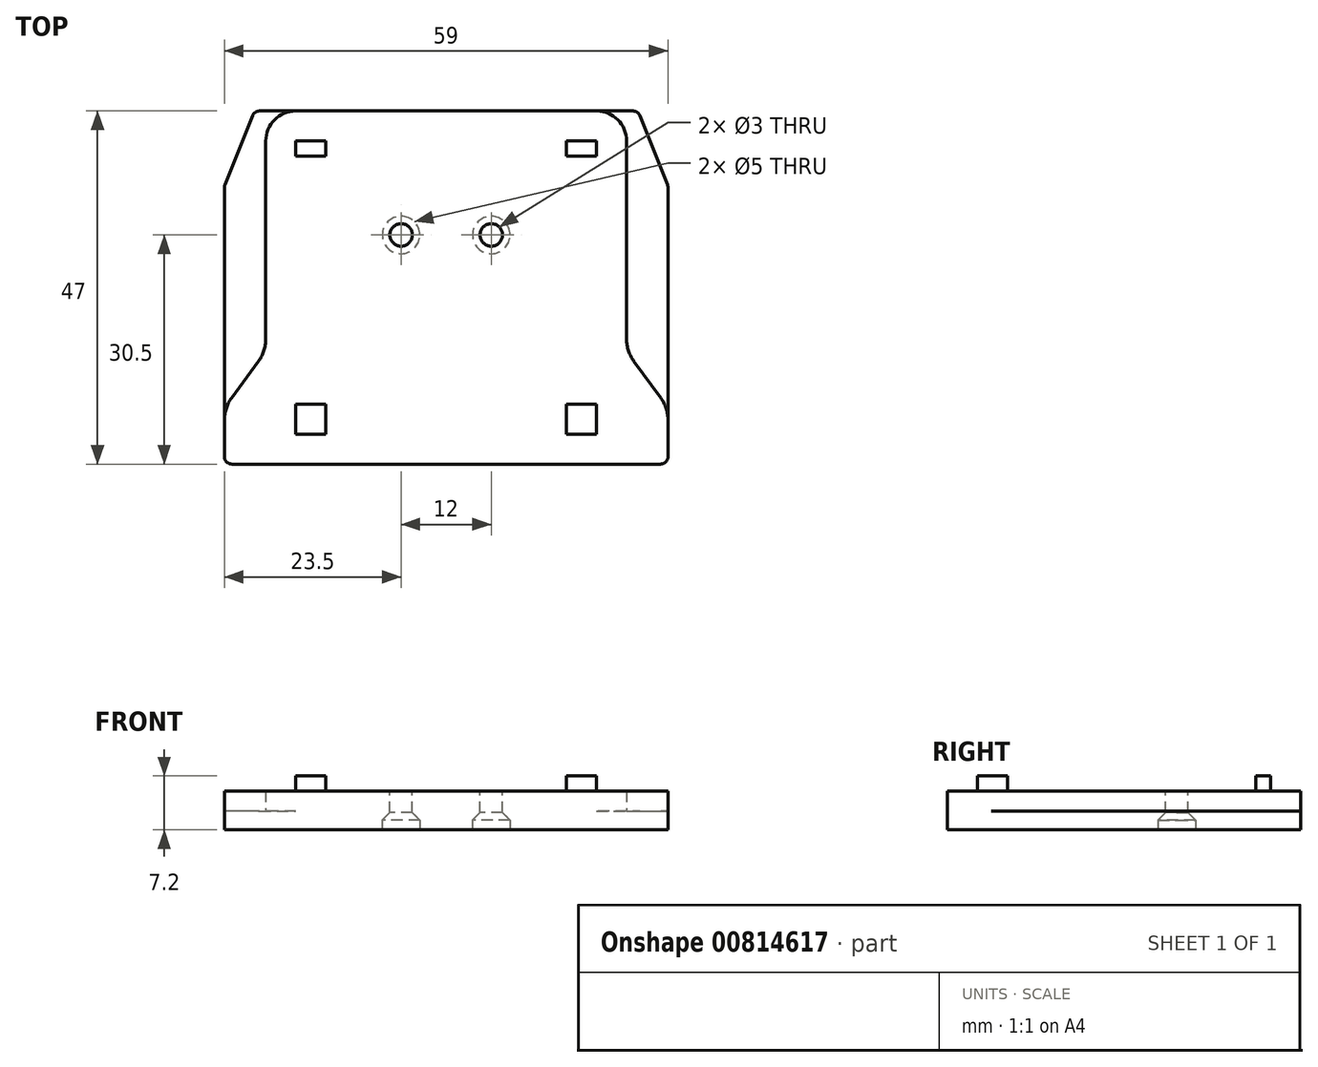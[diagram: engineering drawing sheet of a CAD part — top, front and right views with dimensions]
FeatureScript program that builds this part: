
annotation { "Feature Type Name" : "Feature", "Feature Type Description" : "" }
export const myFeature = defineFeature(function(context is Context, id is Id, definition is map)
    precondition{}
    {
        {
            var Q0;
            Q0=qCreatedBy(makeId("Top.planeOp"),FACE);
            var sketch = newSketch(context, id + "F0", { "sketchPlane" : qUnion([Q0])});
            skLineSegment(sketch, "E0.bottom", {"start": v(4, 0) * mm, "end": v(55, 0) * mm});
            skLineSegment(sketch, "E0.top", {"start": v(0, -47) * mm, "end": v(59, -47) * mm});
            skLineSegment(sketch, "E0.left", {"start": v(0, -10) * mm, "end": v(0, -47) * mm});
            skLineSegment(sketch, "E0.right", {"start": v(59, -10) * mm, "end": v(59, -47) * mm});
            skLineSegment(sketch, "E1", {"start": v(4, 0) * mm, "end": v(0, -10) * mm});
            skPoint(sketch, "E2.orphan", {"position": v(0, 0) * mm});
            skLineSegment(sketch, "E3", {"start": v(55, 0) * mm, "end": v(59, -10) * mm});
            skPoint(sketch, "E4.orphan", {"position": v(59, 0) * mm});
            skSolve(sketch);
        }
        {
            var Q0;
            Q0=makeQuery(id+"F0.imprint","IMPRINT",FACE,{"disambiguationData":[TD([[makeQuery(id+"F0.imprint","IMPRINT",EDGE,{"derivedFrom":sQuery(id+"F0.wireOp",EDGE,"E0.bottom")}),-1.0]])]});
            extrude(context, id + "F1", {"entities" : qUnion([Q0]), "depth" : 2.5 * mm, "offsetDistance" : 25 * mm});
        }
        {
            var Q0;
            Q0=makeQuery(id+"F1.opExtrude","CAP_FACE",FACE,{"disambiguationData":[OSD([sQuery(id+"F0.wireOp",EDGE,"E0.bottom"),sQuery(id+"F0.wireOp",EDGE,"E0.top"),sQuery(id+"F0.wireOp",EDGE,"E0.left"),sQuery(id+"F0.wireOp",EDGE,"E0.right"),sQuery(id+"F0.wireOp",EDGE,"E1"),sQuery(id+"F0.wireOp",EDGE,"E3")])],"isStart":false});
            var sketch = newSketch(context, id + "F2", { "sketchPlane" : qUnion([Q0])});
            skLineSegment(sketch, "E5.bottom", {"start": v(0, -47) * mm, "end": v(59, -47) * mm});
            skLineSegment(sketch, "E5.left", {"start": v(0, -47) * mm, "end": v(0, -39.5) * mm});
            skLineSegment(sketch, "E5.right", {"start": v(59, -47) * mm, "end": v(59, -39.5) * mm});
            skLineSegment(sketch, "E6.top", {"start": v(9.5, 0) * mm, "end": v(49.5, 0) * mm});
            skLineSegment(sketch, "E6.left", {"start": v(5.5, -32) * mm, "end": v(5.5, -4) * mm});
            skLineSegment(sketch, "E6.right", {"start": v(53.5, -32) * mm, "end": v(53.5, -4) * mm});
            skPoint(sketch, "E7.visualSharp", {"position": v(5.5, 0) * mm});
            skArc(sketch, "E7.filletArc", {"start": v(9.5, 0) * mm, "mid": v(6.67, -1.17) * mm, "end": v(5.5, -4) * mm});
            skPoint(sketch, "E8.visualSharp", {"position": v(53.5, 0) * mm});
            skArc(sketch, "E8.filletArc", {"start": v(53.5, -4) * mm, "mid": v(52.33, -1.17) * mm, "end": v(49.5, 0) * mm});
            skLineSegment(sketch, "E9", {"start": v(53.5, -32) * mm, "end": v(59, -39.5) * mm});
            skLineSegment(sketch, "E10", {"start": v(5.5, -32) * mm, "end": v(0, -39.5) * mm});
            skPoint(sketch, "E11.orphan", {"position": v(0, -32) * mm});
            skPoint(sketch, "E12.orphan", {"position": v(59, -32) * mm});
            skSolve(sketch);
        }
        {
            var Q0;
            Q0=makeQuery(id+"F2.imprint","IMPRINT",FACE,{"disambiguationData":[TD([[makeQuery(id+"F2.imprint","IMPRINT",EDGE,{"derivedFrom":sQuery(id+"F2.wireOp",EDGE,"E5.bottom")}),1.0]])]});
            extrude(context, id + "F3", {"entities" : qUnion([Q0]), "operationType" : NewBodyOperationType.ADD, "depth" : 2.7 * mm, "offsetDistance" : 25 * mm});
        }
        {
            var Q0;
            Q0=makeQuery(id+"F3.boolean.opBoolean","MERGE",EDGE,{"derivedFrom":[makeQuery(id+"F1.opExtrude","SWEPT_EDGE",EDGE,{"disambiguationData":[OSD([sQuery(id+"F0.wireOp",EDGE,"E0.top"),sQuery(id+"F0.wireOp",EDGE,"E0.left")])]}),makeQuery(id+"F3.opExtrude","SWEPT_EDGE",EDGE,{"disambiguationData":[OSD([sQuery(id+"F2.wireOp",EDGE,"E5.bottom"),sQuery(id+"F2.wireOp",EDGE,"E5.left")])]})]});
            var Q1;
            Q1=makeQuery(id+"F3.boolean.opBoolean","MERGE",EDGE,{"derivedFrom":[makeQuery(id+"F1.opExtrude","SWEPT_EDGE",EDGE,{"disambiguationData":[OSD([sQuery(id+"F0.wireOp",EDGE,"E0.top"),sQuery(id+"F0.wireOp",EDGE,"E0.right")])]}),makeQuery(id+"F3.opExtrude","SWEPT_EDGE",EDGE,{"disambiguationData":[OSD([sQuery(id+"F2.wireOp",EDGE,"E5.bottom"),sQuery(id+"F2.wireOp",EDGE,"E5.right")])]})]});
            var Q2;
            Q2=makeQuery(id+"F1.opExtrude","SWEPT_EDGE",EDGE,{"disambiguationData":[OSD([sQuery(id+"F0.wireOp",EDGE,"E0.bottom"),sQuery(id+"F0.wireOp",EDGE,"E1")])]});
            var Q3;
            Q3=makeQuery(id+"F1.opExtrude","SWEPT_EDGE",EDGE,{"disambiguationData":[OSD([sQuery(id+"F0.wireOp",EDGE,"E0.bottom"),sQuery(id+"F0.wireOp",EDGE,"E3")])]});
            var Q4;
            Q4=makeQuery(id+"F1.opExtrude","SWEPT_EDGE",EDGE,{"disambiguationData":[OSD([sQuery(id+"F0.wireOp",EDGE,"E0.right"),sQuery(id+"F0.wireOp",EDGE,"E3")])]});
            var Q5;
            Q5=makeQuery(id+"F1.opExtrude","SWEPT_EDGE",EDGE,{"disambiguationData":[OSD([sQuery(id+"F0.wireOp",EDGE,"E0.left"),sQuery(id+"F0.wireOp",EDGE,"E1")])]});
            fillet(context, id + "F4", {"entities" : qUnion([Q0, Q1, Q2, Q3, Q4, Q5]), "radius" : 1 * mm, "tangentPropagation" : true, "allowEdgeOverflow" : false});
        }
        {
            var Q0;
            Q0=makeQuery(id+"F3.opExtrude","SWEPT_EDGE",EDGE,{"disambiguationData":[OSD([sQuery(id+"F0.wireOp",EDGE,"E0.left"),sQuery(id+"F2.wireOp",EDGE,"E5.left"),sQuery(id+"F2.wireOp",EDGE,"E10")])]});
            var Q1;
            Q1=makeQuery(id+"F3.opExtrude","SWEPT_EDGE",EDGE,{"disambiguationData":[OSD([sQuery(id+"F0.wireOp",EDGE,"E0.right"),sQuery(id+"F2.wireOp",EDGE,"E5.right"),sQuery(id+"F2.wireOp",EDGE,"E9")])]});
            var Q2;
            Q2=makeQuery(id+"F3.opExtrude","SWEPT_EDGE",EDGE,{"disambiguationData":[OSD([sQuery(id+"F2.wireOp",EDGE,"E6.right"),sQuery(id+"F2.wireOp",EDGE,"E9")])]});
            var Q3;
            Q3=makeQuery(id+"F3.opExtrude","SWEPT_EDGE",EDGE,{"disambiguationData":[OSD([sQuery(id+"F2.wireOp",EDGE,"E6.left"),sQuery(id+"F2.wireOp",EDGE,"E10")])]});
            fillet(context, id + "F5", {"entities" : qUnion([Q0, Q1, Q2, Q3]), "radius" : 5 * mm, "tangentPropagation" : true, "allowEdgeOverflow" : false});
        }
        {
            var Q0;
            Q0=makeQuery(id+"F3.opExtrude","CAP_FACE",FACE,{"disambiguationData":[OSD([sQuery(id+"F2.wireOp",EDGE,"E5.bottom"),sQuery(id+"F2.wireOp",EDGE,"E5.left"),sQuery(id+"F2.wireOp",EDGE,"E5.right"),sQuery(id+"F2.wireOp",EDGE,"E6.top"),sQuery(id+"F2.wireOp",EDGE,"E6.left"),sQuery(id+"F2.wireOp",EDGE,"E6.right"),sQuery(id+"F2.wireOp",EDGE,"E7.filletArc"),sQuery(id+"F2.wireOp",EDGE,"E8.filletArc"),sQuery(id+"F2.wireOp",EDGE,"E9"),sQuery(id+"F2.wireOp",EDGE,"E10")])],"isStart":false});
            var sketch = newSketch(context, id + "F6", { "sketchPlane" : qUnion([Q0])});
            skLineSegment(sketch, "E13.bottom", {"start": v(9.5, -4) * mm, "end": v(13.5, -4) * mm});
            skLineSegment(sketch, "E13.top", {"start": v(9.5, -6) * mm, "end": v(13.5, -6) * mm});
            skLineSegment(sketch, "E13.left", {"start": v(9.5, -4) * mm, "end": v(9.5, -6) * mm});
            skLineSegment(sketch, "E13.right", {"start": v(13.5, -4) * mm, "end": v(13.5, -6) * mm});
            skLineSegment(sketch, "E14.bottom", {"start": v(9.5, -39) * mm, "end": v(13.5, -39) * mm});
            skLineSegment(sketch, "E14.top", {"start": v(9.5, -43) * mm, "end": v(13.5, -43) * mm});
            skLineSegment(sketch, "E14.left", {"start": v(9.5, -39) * mm, "end": v(9.5, -43) * mm});
            skLineSegment(sketch, "E14.right", {"start": v(13.5, -39) * mm, "end": v(13.5, -43) * mm});
            skLineSegment(sketch, "E15.bottom", {"start": v(45.5, -4) * mm, "end": v(49.5, -4) * mm});
            skLineSegment(sketch, "E15.top", {"start": v(45.5, -6) * mm, "end": v(49.5, -6) * mm});
            skLineSegment(sketch, "E15.left", {"start": v(45.5, -4) * mm, "end": v(45.5, -6) * mm});
            skLineSegment(sketch, "E15.right", {"start": v(49.5, -4) * mm, "end": v(49.5, -6) * mm});
            skLineSegment(sketch, "E16.bottom", {"start": v(45.5, -39) * mm, "end": v(49.5, -39) * mm});
            skLineSegment(sketch, "E16.top", {"start": v(45.5, -43) * mm, "end": v(49.5, -43) * mm});
            skLineSegment(sketch, "E16.left", {"start": v(45.5, -39) * mm, "end": v(45.5, -43) * mm});
            skLineSegment(sketch, "E16.right", {"start": v(49.5, -39) * mm, "end": v(49.5, -43) * mm});
            skSolve(sketch);
        }
        {
            var Q0;
            Q0=qSketchRegion(id+"F6",true);
            extrude(context, id + "F7", {"entities" : qUnion([Q0]), "operationType" : NewBodyOperationType.ADD, "depth" : 2 * mm, "offsetDistance" : 25 * mm});
        }
        {
            var Q0;
            Q0=makeQuery(id+"F6.imprint","IMPRINT",FACE,{"disambiguationData":[TD([[makeQuery(id+"F6.imprint","IMPRINT",EDGE,{"derivedFrom":sQuery(id+"F6.wireOp",EDGE,"E13.bottom")}),1.0]])]});
            var sketch = newSketch(context, id + "F8", { "sketchPlane" : qUnion([Q0])});
            skCircle(sketch, "E17", {"center": v(23.5, -16.5) * mm, "radius": 1.5 * mm});
            skCircle(sketch, "E18", {"center": v(35.5, -16.5) * mm, "radius": 1.5 * mm});
            skSolve(sketch);
        }
        {
            var Q0;
            Q0=qSketchRegion(id+"F8",true);
            extrude(context, id + "F9", {"entities" : qUnion([Q0]), "operationType" : NewBodyOperationType.REMOVE, "oppositeDirection" : true, "depth" : 6 * mm, "offsetDistance" : 25 * mm});
        }
        {
            var Q0;
            Q0=makeQuery(id+"F0.imprint","IMPRINT",FACE,{"disambiguationData":[TD([[makeQuery(id+"F0.imprint","IMPRINT",EDGE,{"derivedFrom":sQuery(id+"F0.wireOp",EDGE,"E0.bottom")}),-1.0]])]});
            var sketch = newSketch(context, id + "F10", { "sketchPlane" : qUnion([Q0])});
            skCircle(sketch, "E19", {"center": v(35.5, -16.5) * mm, "radius": 2.5 * mm});
            skCircle(sketch, "E20", {"center": v(23.5, -16.5) * mm, "radius": 2.5 * mm});
            skSolve(sketch);
        }
        {
            var Q0;
            Q0=qSketchRegion(id+"F10",true);
            extrude(context, id + "F11", {"entities" : qUnion([Q0]), "operationType" : NewBodyOperationType.REMOVE, "depth" : 2.5 * mm, "offsetDistance" : 25 * mm});
        }
        {
            var Q0;
            Q0=makeQuery(id+"F11.boolean.opBoolean","COPY",EDGE,{"derivedFrom":makeQuery(id+"F11.opExtrude","CAP_EDGE",EDGE,{"disambiguationData":[OSD([sQuery(id+"F10.wireOp",EDGE,"E19")])],"isStart":false})});
            var Q1;
            Q1=makeQuery(id+"F11.boolean.opBoolean","COPY",EDGE,{"derivedFrom":makeQuery(id+"F11.opExtrude","CAP_EDGE",EDGE,{"disambiguationData":[OSD([sQuery(id+"F10.wireOp",EDGE,"E20")])],"isStart":false})});
            chamfer(context, id + "F12", {"entities" : qUnion([Q0, Q1]), "width" : 1.2 * mm, "tangentPropagation" : true});
        }
    });
